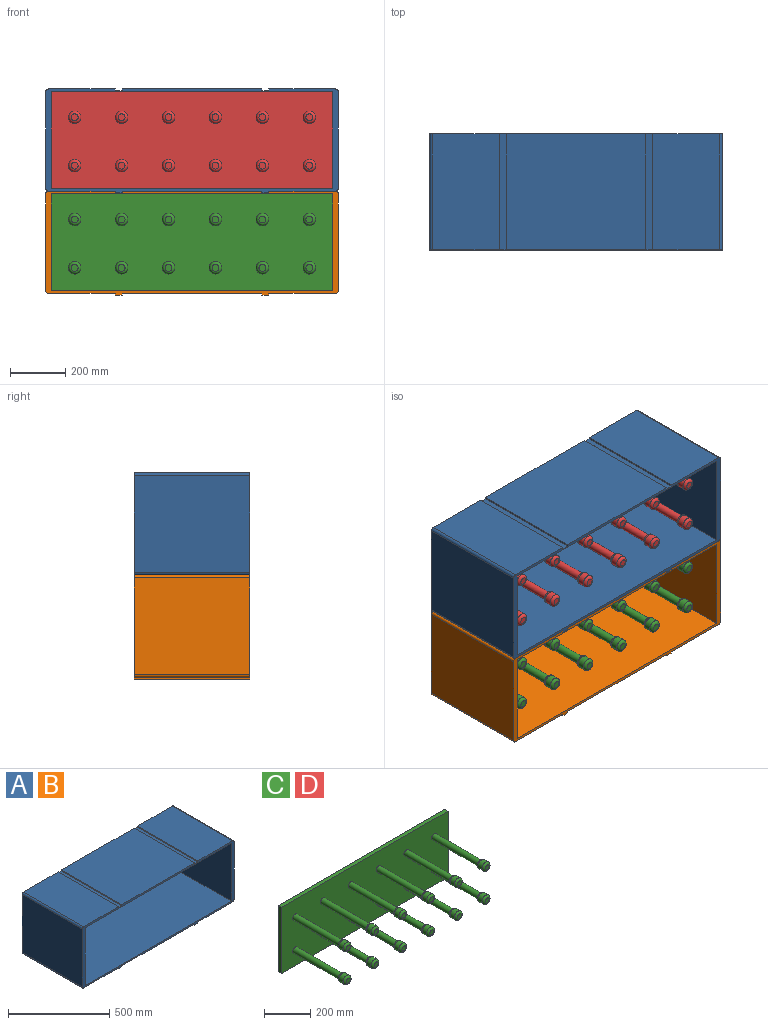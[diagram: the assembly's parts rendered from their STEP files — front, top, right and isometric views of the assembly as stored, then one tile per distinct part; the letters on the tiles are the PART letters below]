
ASSEMBLY  parts=4 mates=3
PART A: 43 faces, bbox 1060x420x376 mm
  f0: plane 1060x376mm, normal (0,1,0), area 363314.2mm2, adj f1,f2,f3,f4,f6,f7,f8,f9
  f1: plane 505x420mm, normal (0,0,-1), area 212100mm2, adj f0,f5,f22,f25
  f2: plane 420x242.5mm, normal (0,0,-1), area 101850mm2, adj f0,f5,f21,f27
  f3: plane 505x420mm, normal (0,0,1), area 212100mm2, adj f0,f5,f16,f18
  f4: plane 420x242.5mm, normal (0,0,1), area 101850mm2, adj f0,f5,f15,f29
  f5: plane 1060x376mm, normal (0,-1,0), area 35114.2mm2, adj f1,f2,f3,f4,f6,f7,f8,f9
  f6: plane 420x242.5mm, normal (0,0,-1), area 101850mm2, adj f0,f5,f24,f30
  f7: plane 420x350mm, normal (1,0,0), area 147000mm2, adj f0,f5,f27,f28
  f8: plane 420x242.5mm, normal (0,0,1), area 101850mm2, adj f0,f5,f19,f28
  f9: plane 420x350mm, normal (-1,0,0), area 147000mm2, adj f0,f5,f29,f30
  f10: plane 1020x400mm, normal (0,0,1), area 408000mm2, adj f5,f11,f13,f14
  f11: plane 400x350mm, normal (-1,0,0), area 140000mm2, adj f5,f10,f12,f14
  f12: plane 1020x400mm, normal (0,0,-1), area 408000mm2, adj f5,f11,f13,f14
  f13: plane 400x350mm, normal (1,0,0), area 140000mm2, adj f5,f10,f12,f14
  f14: plane 1020x350mm, normal (0,-1,0), area 336942.5mm2, adj f10,f11,f12,f13,f41,f42
  f15: plane 420x6mm, normal (1,0,0), area 2520mm2, adj f0,f4,f5,f17
  f16: plane 420x6mm, normal (-1,0,0), area 2520mm2, adj f0,f3,f5,f17
  f17: plane 420x25mm, normal (0,0,1), area 10500mm2, adj f0,f5,f15,f16
  f18: plane 420x6mm, normal (1,0,0), area 2520mm2, adj f0,f3,f5,f20
  f19: plane 420x6mm, normal (-1,0,0), area 2520mm2, adj f0,f5,f8,f20
  f20: plane 420x25mm, normal (0,0,1), area 10500mm2, adj f0,f5,f18,f19
  f21: plane 420x6mm, normal (1,0,0), area 2520mm2, adj f0,f2,f5,f23
  f22: plane 420x6mm, normal (-1,0,0), area 2520mm2, adj f0,f1,f5,f23
  f23: plane 420x25mm, normal (0,0,-1), area 10500mm2, adj f0,f5,f21,f22
  f24: plane 420x6mm, normal (-1,0,0), area 2520mm2, adj f0,f5,f6,f26
  f25: plane 420x6mm, normal (1,0,0), area 2520mm2, adj f0,f1,f5,f26
  f26: plane 420x25mm, normal (0,0,-1), area 10500mm2, adj f0,f5,f24,f25
  f27: cylinder r=10mm len=420mm, axis (0,1,0), area 6597.3mm2, adj f0,f2,f5,f7
  f28: cylinder r=10mm len=420mm, axis (0,-1,0), area 6597.3mm2, adj f0,f5,f7,f8
  f29: cylinder r=10mm len=420mm, axis (0,1,0), area 6597.3mm2, adj f0,f4,f5,f9
  f30: cylinder r=10mm len=420mm, axis (0,-1,0), area 6597.3mm2, adj f0,f5,f6,f9
  f31: plane 120x2mm, normal (1,0,0), area 240mm2, adj f0,f32,f34,f35
  f32: plane 120x2mm, normal (0,0,-1), area 240mm2, adj f0,f31,f33,f35
  f33: plane 120x2mm, normal (-1,0,0), area 240mm2, adj f0,f32,f34,f35
  f34: plane 120x2mm, normal (0,0,1), area 240mm2, adj f0,f31,f33,f35
  f35: plane 120x120mm, normal (0,1,0), area 4371.3mm2, adj f31,f32,f33,f34,f42
  f36: plane 120x2mm, normal (0,0,1), area 240mm2, adj f0,f37,f39,f40
  f37: plane 120x2mm, normal (1,0,0), area 240mm2, adj f0,f36,f38,f40
  f38: plane 120x2mm, normal (0,0,-1), area 240mm2, adj f0,f37,f39,f40
  f39: plane 120x2mm, normal (-1,0,0), area 240mm2, adj f0,f36,f38,f40
  f40: plane 120x120mm, normal (0,1,0), area 4371.3mm2, adj f36,f37,f38,f39,f41
  f41: cylinder r=56.5mm len=113mm, axis (0,1,0), area 6390mm2, adj f14,f40
  f42: cylinder r=56.5mm len=113mm, axis (0,1,0), area 6390mm2, adj f14,f35
PART B: same geometry as A
PART C: 66 faces, bbox 1020x345x350 mm
  f0: plane 1020x20mm, normal (0,0,-1), area 20400mm2, adj f1,f3,f4,f5
  f1: plane 350x20mm, normal (1,0,0), area 7000mm2, adj f0,f2,f4,f5
  f2: plane 1020x20mm, normal (0,0,1), area 20400mm2, adj f1,f3,f4,f5
  f3: plane 350x20mm, normal (-1,0,0), area 7000mm2, adj f0,f2,f4,f5
  f4: plane 1020x350mm, normal (0,1,0), area 357000mm2, adj f0,f1,f2,f3
  f5: plane 1020x350mm, normal (0,-1,0), area 348517.7mm2, adj f0,f1,f2,f3,f6,f7,f8,f9
  f6: cylinder r=15mm len=280mm, axis (0,1,0), area 26389.4mm2, adj f5,f42
  f7: cylinder r=15mm len=280mm, axis (0,1,0), area 26389.4mm2, adj f5,f64
  f8: cylinder r=15mm len=280mm, axis (0,1,0), area 26389.4mm2, adj f5,f62
  f9: cylinder r=15mm len=280mm, axis (0,1,0), area 26389.4mm2, adj f5,f60
  f10: cylinder r=15mm len=280mm, axis (0,1,0), area 26389.4mm2, adj f5,f58
  f11: cylinder r=15mm len=280mm, axis (0,1,0), area 26389.4mm2, adj f5,f56
  f12: cylinder r=15mm len=280mm, axis (0,1,0), area 26389.4mm2, adj f5,f54
  f13: cylinder r=15mm len=280mm, axis (0,1,0), area 26389.4mm2, adj f5,f52
  f14: cylinder r=15mm len=280mm, axis (0,1,0), area 26389.4mm2, adj f5,f50
  f15: cylinder r=15mm len=280mm, axis (0,1,0), area 26389.4mm2, adj f5,f48
  f16: cylinder r=15mm len=280mm, axis (0,1,0), area 26389.4mm2, adj f5,f46
  f17: cylinder r=15mm len=280mm, axis (0,1,0), area 26389.4mm2, adj f5,f44
  f18: cylinder r=22.5mm len=45mm, axis (0,1,0), area 3579.2mm2, adj f42,f43
  f19: plane 25x25mm, normal (0,-1,0), area 490.9mm2, adj f43
  f20: cylinder r=22.5mm len=45mm, axis (0,1,0), area 3579.2mm2, adj f64,f65
  f21: plane 25x25mm, normal (0,-1,0), area 490.9mm2, adj f65
  f22: cylinder r=22.5mm len=45mm, axis (0,1,0), area 3579.2mm2, adj f62,f63
  f23: plane 25x25mm, normal (0,-1,0), area 490.9mm2, adj f63
  f24: cylinder r=22.5mm len=45mm, axis (0,1,0), area 3579.2mm2, adj f60,f61
  f25: plane 25x25mm, normal (0,-1,0), area 490.9mm2, adj f61
  f26: cylinder r=22.5mm len=45mm, axis (0,1,0), area 3579.2mm2, adj f58,f59
  f27: plane 25x25mm, normal (0,-1,0), area 490.9mm2, adj f59
  f28: cylinder r=22.5mm len=45mm, axis (0,1,0), area 3579.2mm2, adj f56,f57
  f29: plane 25x25mm, normal (0,-1,0), area 490.9mm2, adj f57
  f30: cylinder r=22.5mm len=45mm, axis (0,1,0), area 3579.2mm2, adj f54,f55
  f31: plane 25x25mm, normal (0,-1,0), area 490.9mm2, adj f55
  f32: cylinder r=22.5mm len=45mm, axis (0,1,0), area 3579.2mm2, adj f52,f53
  f33: plane 25x25mm, normal (0,-1,0), area 490.9mm2, adj f53
  f34: cylinder r=22.5mm len=45mm, axis (0,1,0), area 3579.2mm2, adj f50,f51
  f35: plane 25x25mm, normal (0,-1,0), area 490.9mm2, adj f51
  f36: cylinder r=22.5mm len=45mm, axis (0,1,0), area 3579.2mm2, adj f48,f49
  f37: plane 25x25mm, normal (0,-1,0), area 490.9mm2, adj f49
  f38: cylinder r=22.5mm len=45mm, axis (0,1,0), area 3579.2mm2, adj f46,f47
  f39: plane 25x25mm, normal (0,-1,0), area 490.9mm2, adj f47
  f40: cylinder r=22.5mm len=45mm, axis (0,1,0), area 3579.2mm2, adj f44,f45
  f41: plane 25x25mm, normal (0,-1,0), area 490.9mm2, adj f45
  f42: torus R=12.5mm, axis (0,1,0), area 1643.6mm2, adj f6,f18
  f43: torus R=12.5mm, axis (0,-1,0), area 1862mm2, adj f18,f19
  f44: torus R=12.5mm, axis (0,1,0), area 1643.6mm2, adj f17,f40
  f45: torus R=12.5mm, axis (0,-1,0), area 1862mm2, adj f40,f41
  f46: torus R=12.5mm, axis (0,1,0), area 1643.6mm2, adj f16,f38
  f47: torus R=12.5mm, axis (0,-1,0), area 1862mm2, adj f38,f39
  f48: torus R=12.5mm, axis (0,1,0), area 1643.6mm2, adj f15,f36
  f49: torus R=12.5mm, axis (0,-1,0), area 1862mm2, adj f36,f37
  f50: torus R=12.5mm, axis (0,1,0), area 1643.6mm2, adj f14,f34
  f51: torus R=12.5mm, axis (0,-1,0), area 1862mm2, adj f34,f35
  f52: torus R=12.5mm, axis (0,1,0), area 1643.6mm2, adj f13,f32
  f53: torus R=12.5mm, axis (0,-1,0), area 1862mm2, adj f32,f33
  f54: torus R=12.5mm, axis (0,1,0), area 1643.6mm2, adj f12,f30
  f55: torus R=12.5mm, axis (0,-1,0), area 1862mm2, adj f30,f31
  f56: torus R=12.5mm, axis (0,1,0), area 1643.6mm2, adj f11,f28
  f57: torus R=12.5mm, axis (0,-1,0), area 1862mm2, adj f28,f29
  f58: torus R=12.5mm, axis (0,1,0), area 1643.6mm2, adj f10,f26
  f59: torus R=12.5mm, axis (0,-1,0), area 1862mm2, adj f26,f27
  f60: torus R=12.5mm, axis (0,1,0), area 1643.6mm2, adj f9,f24
  f61: torus R=12.5mm, axis (0,-1,0), area 1862mm2, adj f24,f25
  f62: torus R=12.5mm, axis (0,1,0), area 1643.6mm2, adj f8,f22
  f63: torus R=12.5mm, axis (0,-1,0), area 1862mm2, adj f22,f23
  f64: torus R=12.5mm, axis (0,1,0), area 1643.6mm2, adj f7,f20
  f65: torus R=12.5mm, axis (0,-1,0), area 1862mm2, adj f20,f21
PART D: same geometry as C
PLACE A t=(1202.88,254.99,-341.25)mm
PLACE B t=(1202.88,254.99,-711.25)mm
PLACE C rot(axis=(-0.35,0.39,0.85),0deg) t=(1202.88,634.99,-711.25)mm
PLACE D t=(1202.88,634.99,-341.25)mm
MATE fastened B.f17 <-> A.f26  axis (0,0,1) through (937.88,254.99,-532.25)mm
MATE fastened D.f4 <-> A.f14  axis (0,1,0) through (1202.88,654.99,-341.25)mm
MATE fastened C.f4 <-> B.f14  axis (0,1,0) through (1202.88,654.99,-711.25)mm
